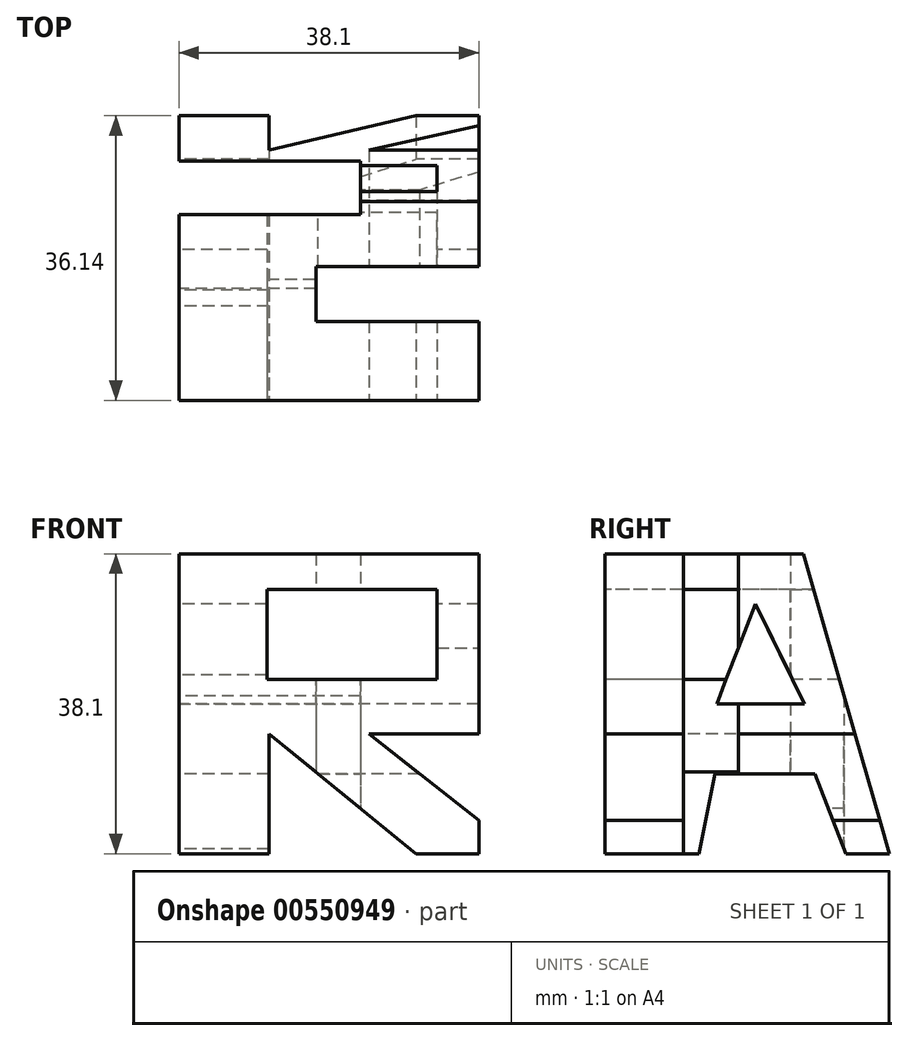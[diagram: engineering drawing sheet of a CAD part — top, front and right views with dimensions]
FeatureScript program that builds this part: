
annotation { "Feature Type Name" : "Feature", "Feature Type Description" : "" }
export const myFeature = defineFeature(function(context is Context, id is Id, definition is map)
    precondition{}
    {
        {
            var Q0;
            Q0=qCreatedBy(makeId("Front.planeOp"),FACE);
            var sketch = newSketch(context, id + "F0", { "sketchPlane" : qUnion([Q0])});
            skLineSegment(sketch, "E0.bottom", {"start": v(0, 0) * mm, "end": v(-38.1, 0) * mm});
            skLineSegment(sketch, "E0.top", {"start": v(0, 38.1) * mm, "end": v(-38.1, 38.1) * mm});
            skLineSegment(sketch, "E0.left", {"start": v(0, 0) * mm, "end": v(0, 38.1) * mm});
            skLineSegment(sketch, "E0.right", {"start": v(-38.1, 0) * mm, "end": v(-38.1, 38.1) * mm});
            skSolve(sketch);
        }
        {
            var Q0;
            Q0=makeQuery(id+"F0.imprint","IMPRINT",FACE,{"disambiguationData":[TD([[makeQuery(id+"F0.imprint","IMPRINT",EDGE,{"derivedFrom":sQuery(id+"F0.wireOp",EDGE,"E0.bottom")}),-1.0]])]});
            extrude(context, id + "F1", {"entities" : qUnion([Q0]), "depth" : 38.1 * mm, "offsetDistance" : 25.4 * mm});
        }
        {
            var Q0;
            Q0=qCreatedBy(makeId("Front.planeOp"),FACE);
            cPlane(context, id + "F2", {"entities" : qUnion([Q0]), "cplaneType" : CPlaneType.OFFSET, "offset" : 38.1 * mm, "width" : 152.4 * mm, "height" : 152.4 * mm});
        }
        {
            var Q0;
            Q0=qCreatedBy(makeId("Right.planeOp"),FACE);
            cPlane(context, id + "F3", {"entities" : qUnion([Q0]), "cplaneType" : CPlaneType.OFFSET, "offset" : 38.1 * mm, "oppositeDirection" : true, "width" : 152.4 * mm, "height" : 152.4 * mm});
        }
        {
            var Q0;
            Q0=qCreatedBy(id+"F2.planeOp",FACE);
            var sketch = newSketch(context, id + "F4", { "sketchPlane" : qUnion([Q0])});
            skLineSegment(sketch, "E1", {"start": v(-38.1, 38.1) * mm, "end": v(-38.1, 0) * mm});
            skLineSegment(sketch, "E2", {"start": v(-38.1, 0) * mm, "end": v(-26.67, 0) * mm});
            skLineSegment(sketch, "E3", {"start": v(0, 0) * mm, "end": v(0, 38.1) * mm});
            skLineSegment(sketch, "E4", {"start": v(0, 38.1) * mm, "end": v(-38.1, 38.1) * mm});
            skPoint(sketch, "E5.end.orphan", {"position": v(-26.67, 15.24) * mm});
            skPoint(sketch, "E6.end.orphan", {"position": v(-22.36, 15.24) * mm});
            skLineSegment(sketch, "E7", {"start": v(-12.88, 0) * mm, "end": v(-16.75, 0) * mm});
            skLineSegment(sketch, "E8.bottom", {"start": v(-176.63, 12.87) * mm, "end": v(-122.05, 12.87) * mm});
            skLineSegment(sketch, "E8.top", {"start": v(-176.63, -32.1) * mm, "end": v(-122.05, -32.1) * mm});
            skLineSegment(sketch, "E8.left", {"start": v(-176.63, 12.87) * mm, "end": v(-176.63, -32.1) * mm});
            skLineSegment(sketch, "E8.right", {"start": v(-122.05, 12.87) * mm, "end": v(-122.05, -32.1) * mm});
            skLineSegment(sketch, "E9", {"start": v(-166.68, -32.1) * mm, "end": v(-166.68, -15.28) * mm});
            skLineSegment(sketch, "E10", {"start": v(-166.68, -15.28) * mm, "end": v(-130.29, -32.1) * mm});
            skLineSegment(sketch, "E11", {"start": v(-130.29, -32.1) * mm, "end": v(-122.05, -32.1) * mm});
            skLineSegment(sketch, "E12", {"start": v(-122.05, -26.27) * mm, "end": v(-157.75, -12.54) * mm});
            skLineSegment(sketch, "E13", {"start": v(-157.75, -12.54) * mm, "end": v(-122.05, -12.54) * mm});
            skLineSegment(sketch, "E14", {"start": v(-157.75, 4.97) * mm, "end": v(-157.75, -4.98) * mm});
            skLineSegment(sketch, "E15", {"start": v(-157.75, -4.98) * mm, "end": v(-133.38, -4.98) * mm});
            skLineSegment(sketch, "E16", {"start": v(-133.38, -4.98) * mm, "end": v(-133.38, 5.32) * mm});
            skLineSegment(sketch, "E17", {"start": v(-133.38, 5.32) * mm, "end": v(-157.75, 4.97) * mm});
            skPoint(sketch, "E18.end.orphan", {"position": v(-25.48, 25.26) * mm});
            skPoint(sketch, "E19.start.orphan", {"position": v(-24.82, 25.26) * mm});
            skPoint(sketch, "E20.start.orphan", {"position": v(-12.88, 34.65) * mm});
            skLineSegment(sketch, "E21", {"start": v(-26.67, 0) * mm, "end": v(-26.67, 15.24) * mm});
            skLineSegment(sketch, "E22", {"start": v(-26.67, 15.24) * mm, "end": v(-7.96, 0) * mm});
            skLineSegment(sketch, "E23", {"start": v(0, 4.24) * mm, "end": v(-13.97, 15.24) * mm});
            skLineSegment(sketch, "E24", {"start": v(-13.97, 15.24) * mm, "end": v(0, 15.24) * mm});
            skLineSegment(sketch, "E25", {"start": v(-5.32, 33.57) * mm, "end": v(-26.9, 33.57) * mm});
            skLineSegment(sketch, "E26", {"start": v(-26.9, 33.57) * mm, "end": v(-26.9, 22.14) * mm});
            skLineSegment(sketch, "E27", {"start": v(-26.9, 22.14) * mm, "end": v(-5.32, 22.14) * mm});
            skLineSegment(sketch, "E28", {"start": v(-5.32, 22.14) * mm, "end": v(-5.32, 33.57) * mm});
            skLineSegment(sketch, "E29", {"start": v(-38.1, 0) * mm, "end": v(0, 0) * mm});
            skSolve(sketch);
        }
        {
            var Q0;
            Q0=makeQuery(id+"F4.imprint","IMPRINT",FACE,{"disambiguationData":[TD([[makeQuery(id+"F4.imprint","IMPRINT",EDGE,{"derivedFrom":sQuery(id+"F4.wireOp",EDGE,"E25")}),1.0]])]});
            var Q1;
            {var subQ0=sQuery(id+"F4.wireOp",EDGE,"E21");Q1=makeQuery(id+"F4.imprint","IMPRINT",FACE,{"disambiguationData":[TD([[makeQuery(id+"F4.imprint","IMPRINT",EDGE,{"derivedFrom":subQ0}),-1.0]])]});}
            var Q2;
            {var subQ0=sQuery(id+"F4.wireOp",EDGE,"E23");Q2=makeQuery(id+"F4.imprint","IMPRINT",FACE,{"disambiguationData":[TD([[makeQuery(id+"F4.imprint","IMPRINT",EDGE,{"derivedFrom":subQ0}),-1.0]])]});}
            extrude(context, id + "F5", {"entities" : qUnion([Q0, Q1, Q2]), "operationType" : NewBodyOperationType.REMOVE, "oppositeDirection" : true, "depth" : 38.1 * mm, "offsetDistance" : 25.4 * mm});
        }
        {
            var Q0;
            Q0=qCreatedBy(id+"F3.planeOp",FACE);
            var sketch = newSketch(context, id + "F6", { "sketchPlane" : qUnion([Q0])});
            skLineSegment(sketch, "E30.bottom", {"start": v(-38.1, 38.1) * mm, "end": v(0, 38.1) * mm});
            skLineSegment(sketch, "E30.top", {"start": v(-38.1, 0) * mm, "end": v(0, 0) * mm});
            skLineSegment(sketch, "E30.left", {"start": v(-38.1, 38.1) * mm, "end": v(-38.1, 0) * mm});
            skLineSegment(sketch, "E30.right", {"start": v(0, 38.1) * mm, "end": v(0, 0) * mm});
            skLineSegment(sketch, "E31", {"start": v(-32.35, 0) * mm, "end": v(-25.59, 38.1) * mm});
            skLineSegment(sketch, "E32", {"start": v(-12.89, 38.1) * mm, "end": v(-1.96, 0) * mm});
            skLineSegment(sketch, "E33", {"start": v(-23.89, 19.05) * mm, "end": v(-12.7, 19.05) * mm});
            skPoint(sketch, "E33.startSnap0", {"position": v(-28.97, 19.05) * mm});
            skLineSegment(sketch, "E34", {"start": v(-12.7, 19.05) * mm, "end": v(-18.98, 31.71) * mm});
            skLineSegment(sketch, "E35", {"start": v(-18.98, 31.71) * mm, "end": v(-23.89, 19.05) * mm});
            skLineSegment(sketch, "E36", {"start": v(-26.15, 0) * mm, "end": v(-24.08, 10.16) * mm});
            skLineSegment(sketch, "E37", {"start": v(-24.08, 10.16) * mm, "end": v(-11.38, 10.16) * mm});
            skLineSegment(sketch, "E38", {"start": v(-32.35, 0) * mm, "end": v(-26.15, 0) * mm});
            skLineSegment(sketch, "E39", {"start": v(-13, 0) * mm, "end": v(-1.96, 0) * mm});
            skLineSegment(sketch, "E40", {"start": v(-25.59, 38.1) * mm, "end": v(-12.89, 38.1) * mm});
            skLineSegment(sketch, "E41", {"start": v(-11.38, 10.16) * mm, "end": v(-7.48, 0) * mm});
            skLineSegment(sketch, "E42", {"start": v(-25.59, 38.1) * mm, "end": v(-32.35, 0) * mm});
            skLineSegment(sketch, "E43", {"start": v(-18.98, 31.71) * mm, "end": v(-12.7, 19.05) * mm});
            skLineSegment(sketch, "E44", {"start": v(-23.89, 19.05) * mm, "end": v(-18.98, 31.71) * mm});
            skLineSegment(sketch, "E45", {"start": v(0, 0) * mm, "end": v(-38.1, 0) * mm});
            skSolve(sketch);
        }
        {
            var Q0;
            {var subQ0=sQuery(id+"F6.wireOp",EDGE,"E30.right");Q0=makeQuery(id+"F6.imprint","IMPRINT",FACE,{"disambiguationData":[TD([[makeQuery(id+"F6.imprint","IMPRINT",EDGE,{"derivedFrom":subQ0}),-1.0]])]});}
            var Q1;
            Q1=makeQuery(id+"F6.imprint","IMPRINT",FACE,{"disambiguationData":[TD([[makeQuery(id+"F6.imprint","IMPRINT",EDGE,{"derivedFrom":sQuery(id+"F6.wireOp",EDGE,"E33")}),1.0]])]});
            var Q2;
            {var subQ0=sQuery(id+"F6.wireOp",EDGE,"E42");Q2=makeQuery(id+"F6.imprint","IMPRINT",FACE,{"disambiguationData":[TD([[makeQuery(id+"F6.imprint","IMPRINT",EDGE,{"derivedFrom":subQ0}),-1.0]])]});}
            var Q3;
            Q3=makeQuery(id+"F6.imprint","IMPRINT",FACE,{"disambiguationData":[TD([[makeQuery(id+"F6.imprint","IMPRINT",EDGE,{"derivedFrom":sQuery(id+"F6.wireOp",EDGE,"E37")}),-1.0]])]});
            extrude(context, id + "F7", {"entities" : qUnion([Q0, Q1, Q2, Q3]), "operationType" : NewBodyOperationType.REMOVE, "depth" : 38.1 * mm, "offsetDistance" : 25.4 * mm});
        }
        {
            var Q0;
            Q0=qCreatedBy(makeId("Top.planeOp"),FACE);
            var sketch = newSketch(context, id + "F8", { "sketchPlane" : qUnion([Q0])});
            skLineSegment(sketch, "E46.bottom", {"start": v(0, 0) * mm, "end": v(-38.1, 0) * mm});
            skLineSegment(sketch, "E46.top", {"start": v(0, -38.1) * mm, "end": v(-38.1, -38.1) * mm});
            skLineSegment(sketch, "E46.left", {"start": v(0, 0) * mm, "end": v(0, -38.1) * mm});
            skLineSegment(sketch, "E46.right", {"start": v(-38.1, 0) * mm, "end": v(-38.1, -38.1) * mm});
            skLineSegment(sketch, "E47", {"start": v(0, -28.08) * mm, "end": v(-20.7, -28.08) * mm});
            skLineSegment(sketch, "E48", {"start": v(-20.7, -28.08) * mm, "end": v(-20.7, -21.14) * mm});
            skLineSegment(sketch, "E49", {"start": v(-20.7, -21.14) * mm, "end": v(0, -21.14) * mm});
            skLineSegment(sketch, "E50", {"start": v(0, -21.14) * mm, "end": v(0, -7.91) * mm});
            skLineSegment(sketch, "E51", {"start": v(0, -7.91) * mm, "end": v(0, 0) * mm});
            skLineSegment(sketch, "E52", {"start": v(-38.1, 0) * mm, "end": v(-38.1, -12.7) * mm});
            skPoint(sketch, "E53.end.orphan", {"position": v(-38.1, -4.27) * mm});
            skLineSegment(sketch, "E54", {"start": v(-38.1, -7.72) * mm, "end": v(-15.03, -7.72) * mm});
            skLineSegment(sketch, "E55", {"start": v(-15.03, -7.72) * mm, "end": v(-15.03, -14.53) * mm});
            skLineSegment(sketch, "E56", {"start": v(-15.03, -14.53) * mm, "end": v(-38.1, -14.53) * mm});
            skSolve(sketch);
        }
        {
            var Q0;
            {var subQ0=sQuery(id+"F8.wireOp",EDGE,"E54");Q0=makeQuery(id+"F8.imprint","IMPRINT",FACE,{"disambiguationData":[TD([[makeQuery(id+"F8.imprint","IMPRINT",EDGE,{"derivedFrom":subQ0}),-1.0]])]});}
            var Q1;
            {var subQ2=sQuery(id+"F8.wireOp",EDGE,"E47");Q1=makeQuery(id+"F8.imprint","IMPRINT",FACE,{"disambiguationData":[TD([[makeQuery(id+"F8.imprint","IMPRINT",EDGE,{"derivedFrom":subQ2}),-1.0]])]});}
            extrude(context, id + "F9", {"entities" : qUnion([Q0, Q1]), "operationType" : NewBodyOperationType.REMOVE, "depth" : 38.1 * mm, "offsetDistance" : 25.4 * mm});
        }
    });
